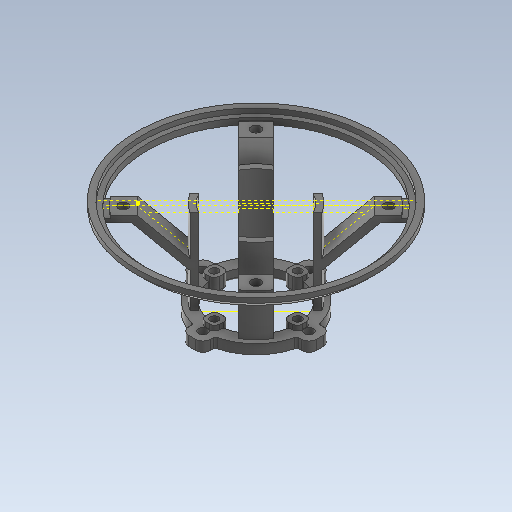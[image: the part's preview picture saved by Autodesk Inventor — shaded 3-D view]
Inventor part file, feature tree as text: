
AUTODESK INVENTOR PART (.ipt)
format: ipt  version: 2020 (Build 240168000, 168)  size: 773,120 bytes
history: native  units: mm
features: projected_geometry x29, sketch x17, extrude x11, other x6, pattern_circular x1, sweep x1, fillet x1
ambient origin geometry x8: Origin, YZ Plane, XZ Plane, XY Plane, X Axis, Y Axis, Z Axis, Center Point
bodies: Body1 (feature_tree)
feature tree (66):
  other  "Твердое тело1"
  sketch  "Эскиз1"
  extrude  "Выдавливание1"  Depth=44.0mm
  extrude  "Выдавливание2"  Depth=3.8mm
  sketch  "Эскиз3"
  extrude  "Выдавливание4"  Depth=40.0mm TaperAngle=360.0deg
  pattern_circular  "Круговой массив1"  [2 undecoded]
  other  "РабПлоскость2"
  sketch  "Эскиз5"
  other  "РабПлоскость1"
  sketch  "Эскиз6"
  sketch  "Эскиз7"
  extrude  "Выдавливание6"  Depth=4.5mm
  sketch  "Эскиз8"
  extrude  "Выдавливание7"  Depth=3.0mm
  sketch  "Эскиз9"
  other  "РабПлоскость3"
  sketch  "Эскиз10"
  sweep  "Сдвиг1"
  extrude  "Выдавливание8"  Depth=1.0mm
  extrude  "Выдавливание9"  TaperAngle=45.0deg  [1 undecoded]
  sketch  "Эскиз14"
  other  "РабПлоскость4"
  sketch  "Эскиз15"
  extrude  "Выдавливание10"  TaperAngle=135.0deg  [1 undecoded]
  extrude  "Выдавливание11"  Depth=34.0mm
  other  "РабПлоскость5"
  sketch  "Эскиз16"
  extrude  "Выдавливание13"  Depth=4.0mm TaperAngle=0.0deg
  extrude  "Выдавливание12"  Depth=3.0mm
  fillet  "Сопряжение1"  [1 undecoded]
  sketch  "Эскиз2"
  sketch  "Эскиз4"
  projected_geometry  "Спроецированная петля1"
  projected_geometry  "Спроецированная петля2"
  projected_geometry  "Спроецированная петля3"
  projected_geometry  "Спроецированная петля4"
  projected_geometry  "Спроецированная петля5"
  projected_geometry  "Спроецированная петля6"
  projected_geometry  "Спроецированная петля7"
  projected_geometry  "Спроецированная петля8"
  projected_geometry  "Спроецированная петля9"
  projected_geometry  "Спроецированная петля10"
  projected_geometry  "Спроецированная петля11"
  projected_geometry  "Спроецированная петля12"
  projected_geometry  "Спроецированная петля13"
  projected_geometry  "Спроецированная петля14"
  projected_geometry  "Спроецированная петля15"
  projected_geometry  "Спроецированная петля16"
  projected_geometry  "Спроецированная петля17"
  projected_geometry  "Спроецированная петля18"
  projected_geometry  "Спроецированная петля19"
  projected_geometry  "Спроецированная петля20"
  sketch  "Эскиз11"
  projected_geometry  "Спроецированная петля21"
  projected_geometry  "Спроецированная петля22"
  projected_geometry  "Спроецированная петля23"
  sketch  "3D эскиз1"
  sketch  "Эскиз12"
  sketch  "Эскиз13"
  projected_geometry  "Спроецированная петля24"
  projected_geometry  "Спроецированная петля25"
  projected_geometry  "Спроецированная петля26"
  projected_geometry  "Спроецированная петля27"
  projected_geometry  "Спроецированная петля28"
  projected_geometry  "Спроецированная петля29"
note: 5 required parameter values undecoded (feature->parameter linkage not recoverable at this tier; creation-order binding heuristic only, values carry confidence <= 0.55)
